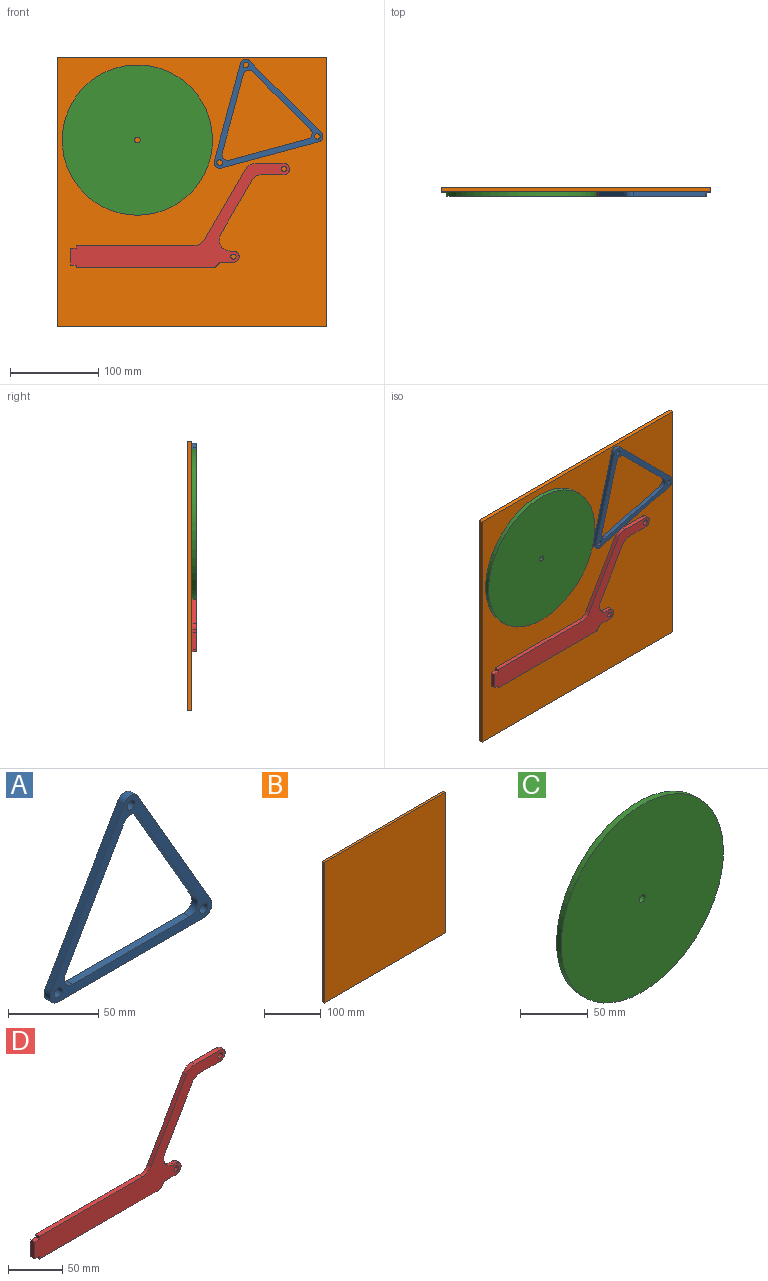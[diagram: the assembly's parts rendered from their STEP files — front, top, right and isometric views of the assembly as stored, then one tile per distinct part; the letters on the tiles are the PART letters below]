
ASSEMBLY  parts=4 mates=1
PART A: 17 faces, bbox 127x4.8x111.7 mm
  f0: plane 98.99x57.15mm, normal (0.87,0,0.5), area 544.4mm2, adj f1,f14,f15,f16
  f1: cylinder r=6.35mm len=11mm, axis (0,1,0), area 63.3mm2, adj f0,f2,f15,f16
  f2: plane 98.99x57.15mm, normal (-0.87,0,0.5), area 544.4mm2, adj f1,f3,f15,f16
  f3: cylinder r=6.35mm len=9.53mm, axis (0,1,0), area 63.3mm2, adj f2,f4,f15,f16
  f4: plane 114.3x4.76mm, normal (0,0,-1), area 544.4mm2, adj f3,f14,f15,f16
  f5: cylinder r=6.35mm len=11mm, axis (0,1,0), area 63.3mm2, adj f6,f13,f15,f16
  f6: plane 79.94x46.15mm, normal (-0.87,0,-0.5), area 439.6mm2, adj f5,f7,f15,f16
  f7: cylinder r=6.35mm len=9.53mm, axis (0,1,0), area 63.3mm2, adj f6,f8,f15,f16
  f8: plane 92.3x4.76mm, normal (0,0,1), area 439.6mm2, adj f7,f9,f15,f16
  f9: cylinder r=6.35mm len=9.53mm, axis (0,1,0), area 63.3mm2, adj f8,f13,f15,f16
  f10: cylinder r=3.17mm len=6.35mm, axis (0,1,0), area 95mm2, adj f15,f16
  f11: cylinder r=3.17mm len=6.35mm, axis (0,1,0), area 95mm2, adj f15,f16
  f12: cylinder r=3.17mm len=6.35mm, axis (0,1,0), area 95mm2, adj f15,f16
  f13: plane 79.94x46.15mm, normal (0.87,0,-0.5), area 439.6mm2, adj f5,f9,f15,f16
  f14: cylinder r=6.35mm len=9.53mm, axis (0,1,0), area 63.3mm2, adj f0,f4,f15,f16
  f15: plane 127x111.69mm, normal (0,-1,0), area 2291.9mm2, adj f0,f1,f2,f3,f4,f5,f6,f7
  f16: plane 127x111.69mm, normal (0,1,0), area 2291.9mm2, adj f0,f1,f2,f3,f4,f5,f6,f7
PART B: 6 faces, bbox 304.8x4.8x304.8 mm
  f0: plane 304.8x4.76mm, normal (-1,0,0), area 1451.6mm2, adj f1,f3,f4,f5
  f1: plane 304.8x4.76mm, normal (0,0,-1), area 1451.6mm2, adj f0,f2,f4,f5
  f2: plane 304.8x4.76mm, normal (1,0,0), area 1451.6mm2, adj f1,f3,f4,f5
  f3: plane 304.8x4.76mm, normal (0,0,1), area 1451.6mm2, adj f0,f2,f4,f5
  f4: plane 304.8x304.8mm, normal (0,-1,0), area 92903mm2, adj f0,f1,f2,f3
  f5: plane 304.8x304.8mm, normal (0,1,0), area 92903mm2, adj f0,f1,f2,f3
PART C: 4 faces, bbox 169.9x4.8x169.9 mm
  f0: cylinder r=3.17mm len=6.35mm, axis (0,1,0), area 95.3mm2, adj f2,f3
  f1: cylinder r=84.93mm len=169.86mm, axis (0,1,0), area 2548.2mm2, adj f2,f3
  f2: plane 169.86x169.86mm, normal (0,-1,0), area 22629.6mm2, adj f0,f1
  f3: plane 169.86x169.86mm, normal (0,1,0), area 22629.6mm2, adj f0,f1
PART D: 25 faces, bbox 247.7x4.8x118 mm
  f0: plane 25.4x4.76mm, normal (0,0,-1), area 121mm2, adj f1,f21,f23,f24
  f1: cylinder r=6.35mm len=12.7mm, axis (0,1,0), area 95mm2, adj f0,f2,f23,f24
  f2: plane 32.73x4.76mm, normal (0,0,1), area 155.9mm2, adj f1,f3,f23,f24
  f3: cylinder r=12.7mm len=11mm, axis (0,1,0), area 63.3mm2, adj f2,f4,f23,f24
  f4: plane 79.94x46.15mm, normal (-0.87,0,0.5), area 439.6mm2, adj f3,f5,f23,f24
  f5: cylinder r=12.7mm len=11mm, axis (0,1,0), area 63.3mm2, adj f4,f6,f23,f24
  f6: plane 134.07x4.76mm, normal (0,0,1), area 638.5mm2, adj f5,f7,f23,f24
  f7: plane 4.76x3.18mm, normal (-1,0,0), area 15.1mm2, adj f6,f8,f23,f24
  f8: plane 6.35x4.76mm, normal (0,0,1), area 30.2mm2, adj f7,f9,f23,f24
  f9: plane 19.05x4.76mm, normal (-1,0,0), area 90.7mm2, adj f8,f10,f23,f24
  f10: plane 6.35x4.76mm, normal (0,0,-1), area 30.2mm2, adj f9,f11,f23,f24
  f11: plane 4.76x3.18mm, normal (-1,0,0), area 15.1mm2, adj f10,f12,f23,f24
  f12: plane 154.1x4.76mm, normal (0,0,-1), area 733.9mm2, adj f11,f13,f23,f24
  f13: cylinder r=6.35mm len=5.5mm, axis (0,1,0), area 31.7mm2, adj f12,f14,f23,f24
  f14: cylinder r=6.35mm len=5.5mm, axis (0,1,0), area 31.7mm2, adj f13,f15,f23,f24
  f15: plane 12.7x4.76mm, normal (0,0,-1), area 60.5mm2, adj f14,f16,f23,f24
  f16: cylinder r=6.35mm len=12.7mm, axis (0,1,0), area 95mm2, adj f15,f17,f23,f24
  f17: plane 4.76x3.4mm, normal (0,0,1), area 16.2mm2, adj f16,f18,f23,f24
  f18: cylinder r=12.7mm len=19.05mm, axis (0,1,0), area 126.7mm2, adj f17,f19,f23,f24
  f19: plane 60.89x35.15mm, normal (0.87,0,-0.5), area 334.8mm2, adj f18,f21,f23,f24
  f20: cylinder r=2.92mm len=5.84mm, axis (0,1,0), area 87.4mm2, adj f23,f24
  f21: cylinder r=12.7mm len=11mm, axis (0,1,0), area 63.3mm2, adj f0,f19,f23,f24
  f22: cylinder r=2.92mm len=5.84mm, axis (0,1,0), area 87.4mm2, adj f23,f24
  f23: plane 247.65x118.04mm, normal (0,-1,0), area 6291.7mm2, adj f0,f1,f2,f3,f4,f5,f6,f7
  f24: plane 247.65x118.04mm, normal (0,1,0), area 6291.7mm2, adj f0,f1,f2,f3,f4,f5,f6,f7
PLACE A rot(axis=(0,-1,0),15deg) t=(58.27,2.38,176.95)mm
PLACE B t=(-125.4,7.15,-8.67)mm
PLACE C t=(-34.76,2.39,202.44)mm
PLACE D t=(73.86,2.38,70.63)mm
MATE planar B.f4 <-> C.f1  axis (0,-1,0) through (27,2.39,143.73)mm
